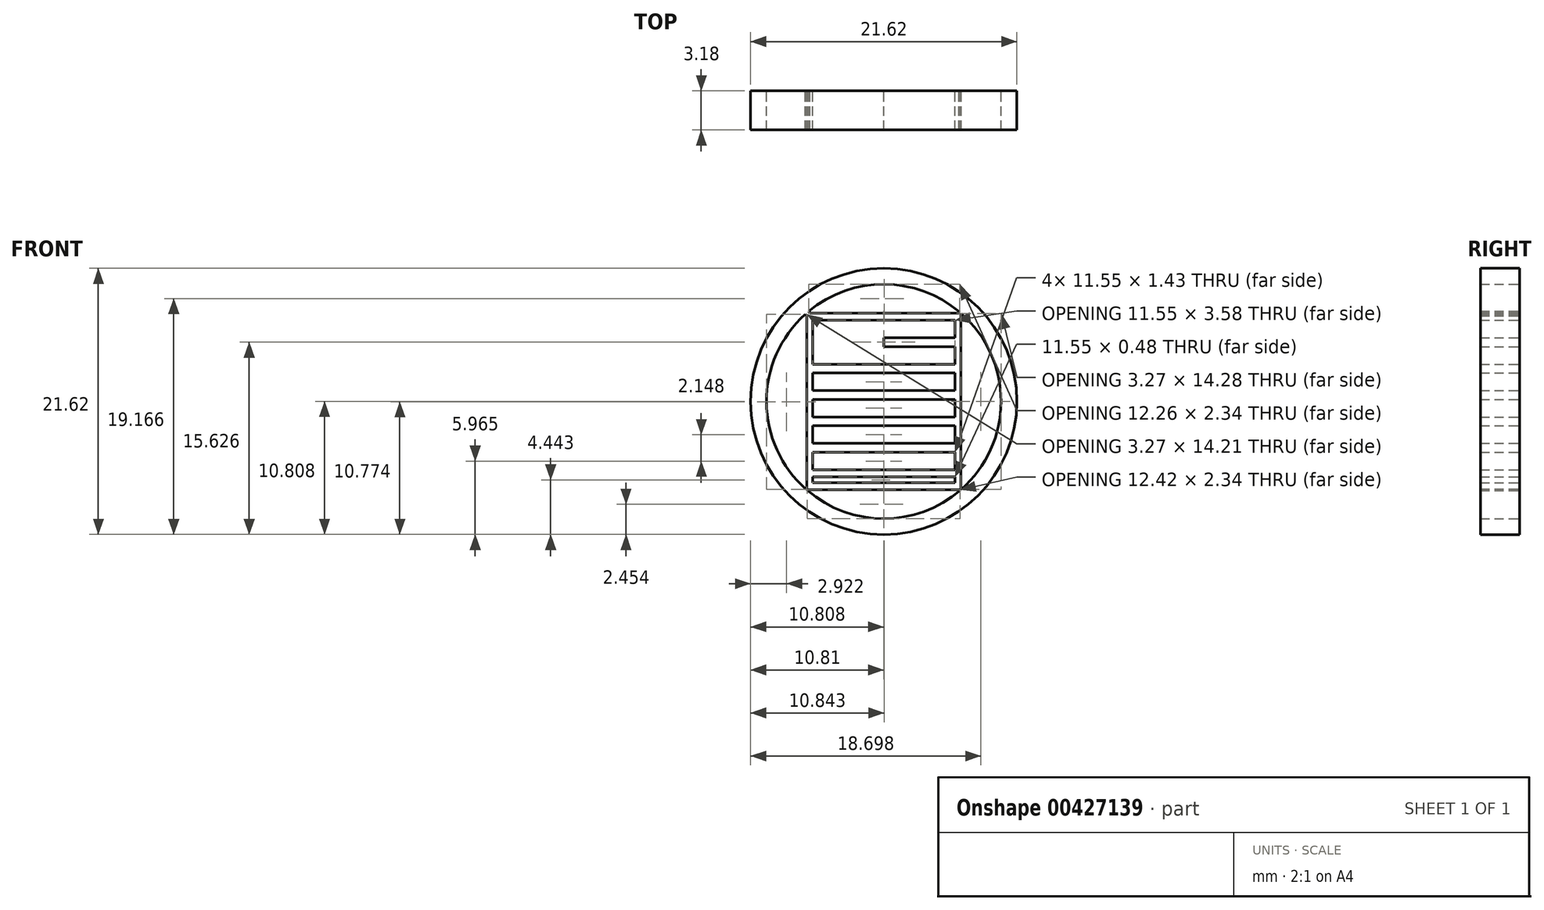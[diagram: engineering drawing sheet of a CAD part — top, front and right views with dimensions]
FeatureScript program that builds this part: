
annotation { "Feature Type Name" : "Feature", "Feature Type Description" : "" }
export const myFeature = defineFeature(function(context is Context, id is Id, definition is map)
    precondition{}
    {
        {
            var Q0;
            Q0=qCreatedBy(makeId("Front.planeOp"),FACE);
            var sketch = newSketch(context, id + "F0", { "sketchPlane" : qUnion([Q0])});
            skCircle(sketch, "E0", {"center": v(0, 0) * mm, "radius": 9.53 * mm});
            skCircle(sketch, "E1", {"center": v(0, 0) * mm, "radius": 10.81 * mm});
            skLineSegment(sketch, "E2", {"start": v(0, 9.53) * mm, "end": v(0, -9.53) * mm});
            skLineSegment(sketch, "E3", {"start": v(-9.53, 0) * mm, "end": v(9.53, 0) * mm});
            skLineSegment(sketch, "E4", {"start": v(-6.25, 7.19) * mm, "end": v(-6.25, -7.19) * mm});
            skLineSegment(sketch, "E5", {"start": v(-6.25, -7.19) * mm, "end": v(6.25, -7.19) * mm});
            skLineSegment(sketch, "E6", {"start": v(6.25, -7.19) * mm, "end": v(6.25, 7.19) * mm});
            skLineSegment(sketch, "E7", {"start": v(6.25, 7.19) * mm, "end": v(-6.25, 7.19) * mm});
            skLineSegment(sketch, "E8", {"start": v(-6.25, 7.19) * mm, "end": v(-5.78, 6.6) * mm});
            skLineSegment(sketch, "E9", {"start": v(-5.78, 6.6) * mm, "end": v(-5.78, -6.6) * mm});
            skLineSegment(sketch, "E10", {"start": v(-5.78, -6.6) * mm, "end": v(-6.25, -7.19) * mm});
            skLineSegment(sketch, "E11", {"start": v(-5.78, -6.6) * mm, "end": v(5.78, -6.6) * mm});
            skLineSegment(sketch, "E12", {"start": v(5.78, -6.6) * mm, "end": v(6.25, -7.19) * mm});
            skLineSegment(sketch, "E13", {"start": v(5.78, -6.6) * mm, "end": v(5.78, 6.6) * mm});
            skLineSegment(sketch, "E14", {"start": v(5.78, 6.6) * mm, "end": v(6.25, 7.19) * mm});
            skLineSegment(sketch, "E15", {"start": v(5.78, 6.6) * mm, "end": v(-5.78, 6.6) * mm});
            skLineSegment(sketch, "E16", {"start": v(-5.78, 5.89) * mm, "end": v(5.78, 5.89) * mm});
            skLineSegment(sketch, "E17", {"start": v(-5.78, 5.17) * mm, "end": v(5.78, 5.17) * mm});
            skLineSegment(sketch, "E18", {"start": v(-5.78, 5.89) * mm, "end": v(-5.78, 5.17) * mm});
            skLineSegment(sketch, "E19", {"start": v(-5.78, 5.89) * mm, "end": v(-5.78, 6.6) * mm});
            skLineSegment(sketch, "E20", {"start": v(-5.78, 4.46) * mm, "end": v(5.78, 4.46) * mm});
            skLineSegment(sketch, "E21", {"start": v(-5.78, 5.17) * mm, "end": v(-5.78, 4.46) * mm});
            skLineSegment(sketch, "E22", {"start": v(-5.78, 3.74) * mm, "end": v(5.78, 3.74) * mm});
            skLineSegment(sketch, "E23", {"start": v(-5.78, 4.46) * mm, "end": v(-5.78, 3.74) * mm});
            skLineSegment(sketch, "E24", {"start": v(-5.78, 3.03) * mm, "end": v(5.78, 3.03) * mm});
            skLineSegment(sketch, "E25", {"start": v(-5.78, 2.31) * mm, "end": v(5.78, 2.31) * mm});
            skLineSegment(sketch, "E26", {"start": v(-5.78, 1.6) * mm, "end": v(5.78, 1.6) * mm});
            skLineSegment(sketch, "E27", {"start": v(-5.78, 0.88) * mm, "end": v(5.78, 0.88) * mm});
            skLineSegment(sketch, "E28", {"start": v(-5.78, 0.16) * mm, "end": v(5.78, 0.16) * mm});
            skLineSegment(sketch, "E29", {"start": v(-5.78, -0.55) * mm, "end": v(5.78, -0.55) * mm});
            skLineSegment(sketch, "E30", {"start": v(-5.78, -1.27) * mm, "end": v(5.78, -1.27) * mm});
            skLineSegment(sketch, "E31", {"start": v(-5.78, -1.98) * mm, "end": v(5.78, -1.98) * mm});
            skLineSegment(sketch, "E32", {"start": v(-5.78, -2.7) * mm, "end": v(5.78, -2.7) * mm});
            skLineSegment(sketch, "E33", {"start": v(-5.78, -3.41) * mm, "end": v(5.78, -3.41) * mm});
            skLineSegment(sketch, "E34", {"start": v(-5.78, -4.13) * mm, "end": v(5.78, -4.13) * mm});
            skLineSegment(sketch, "E35", {"start": v(-5.78, -4.84) * mm, "end": v(5.78, -4.84) * mm});
            skLineSegment(sketch, "E36", {"start": v(-5.78, -5.56) * mm, "end": v(5.78, -5.56) * mm});
            skLineSegment(sketch, "E37", {"start": v(-6.25, 6.94) * mm, "end": v(-6.39, 7.07) * mm});
            skLineSegment(sketch, "E38", {"start": v(-6.1, 7.32) * mm, "end": v(-5.99, 7.19) * mm});
            skLineSegment(sketch, "E39", {"start": v(6.09, 7.19) * mm, "end": v(6.16, 7.26) * mm});
            skLineSegment(sketch, "E40", {"start": v(6.25, 7.07) * mm, "end": v(6.3, 7.14) * mm});
            skLineSegment(sketch, "E41", {"start": v(6.16, -7.19) * mm, "end": v(6.2, -7.22) * mm});
            skLineSegment(sketch, "E42", {"start": v(6.25, -7.1) * mm, "end": v(6.3, -7.14) * mm});
            skLineSegment(sketch, "E43", {"start": v(-6.25, -7.1) * mm, "end": v(-6.3, -7.14) * mm});
            skLineSegment(sketch, "E44", {"start": v(-6.18, -7.19) * mm, "end": v(-6.21, -7.22) * mm});
            skLineSegment(sketch, "E45", {"start": v(5.78, -6.13) * mm, "end": v(-5.78, -6.13) * mm});
            skSolve(sketch);
        }
        {
            var Q0;
            {var subQ5=sQuery(id+"F0.wireOp",EDGE,"E21");Q0=makeQuery(id+"F0.imprint","IMPRINT",FACE,{"disambiguationData":[TD([[makeQuery(id+"F0.imprint","IMPRINT",EDGE,{"derivedFrom":subQ5}),1.0]])]});}
            var Q1;
            {var subQ0=sQuery(id+"F0.wireOp",EDGE,"E17");var subQ1=sQuery(id+"F0.wireOp",EDGE,"E2");var subQ2=makeQuery(id+"F0.imprint","INTERSECT",VERTEX,{"derivedFrom":[subQ1,subQ0]});Q1=makeQuery(id+"F0.imprint","IMPRINT",FACE,{"disambiguationData":[TD([[makeQuery(id+"F0.imprint","IMPRINT",EDGE,{"disambiguationData":[TD([[subQ2,-1.0]])],"derivedFrom":subQ1}),1.0]])]});}
            var Q2;
            {var subQ0=sQuery(id+"F0.wireOp",EDGE,"E24");var subQ1=sQuery(id+"F0.wireOp",EDGE,"E2");var subQ2=makeQuery(id+"F0.imprint","INTERSECT",VERTEX,{"derivedFrom":[subQ1,subQ0]});Q2=makeQuery(id+"F0.imprint","IMPRINT",FACE,{"disambiguationData":[TD([[makeQuery(id+"F0.imprint","IMPRINT",EDGE,{"disambiguationData":[TD([[subQ2,-1.0]])],"derivedFrom":subQ1}),-1.0]])]});}
            var Q3;
            {var subQ0=sQuery(id+"F0.wireOp",EDGE,"E24");var subQ1=sQuery(id+"F0.wireOp",EDGE,"E2");var subQ2=makeQuery(id+"F0.imprint","INTERSECT",VERTEX,{"derivedFrom":[subQ1,subQ0]});Q3=makeQuery(id+"F0.imprint","IMPRINT",FACE,{"disambiguationData":[TD([[makeQuery(id+"F0.imprint","IMPRINT",EDGE,{"disambiguationData":[TD([[subQ2,-1.0]])],"derivedFrom":subQ1}),1.0]])]});}
            var Q4;
            {var subQ0=sQuery(id+"F0.wireOp",EDGE,"E27");var subQ1=sQuery(id+"F0.wireOp",EDGE,"E2");var subQ2=makeQuery(id+"F0.imprint","INTERSECT",VERTEX,{"derivedFrom":[subQ1,subQ0]});Q4=makeQuery(id+"F0.imprint","IMPRINT",FACE,{"disambiguationData":[TD([[makeQuery(id+"F0.imprint","IMPRINT",EDGE,{"disambiguationData":[TD([[subQ2,-1.0]])],"derivedFrom":subQ1}),-1.0]])]});}
            var Q5;
            {var subQ0=sQuery(id+"F0.wireOp",EDGE,"E27");var subQ1=sQuery(id+"F0.wireOp",EDGE,"E2");var subQ2=makeQuery(id+"F0.imprint","INTERSECT",VERTEX,{"derivedFrom":[subQ1,subQ0]});Q5=makeQuery(id+"F0.imprint","IMPRINT",FACE,{"disambiguationData":[TD([[makeQuery(id+"F0.imprint","IMPRINT",EDGE,{"disambiguationData":[TD([[subQ2,-1.0]])],"derivedFrom":subQ1}),1.0]])]});}
            var Q6;
            {var subQ0=sQuery(id+"F0.wireOp",EDGE,"E30");var subQ1=sQuery(id+"F0.wireOp",EDGE,"E2");var subQ2=makeQuery(id+"F0.imprint","INTERSECT",VERTEX,{"derivedFrom":[subQ1,subQ0]});Q6=makeQuery(id+"F0.imprint","IMPRINT",FACE,{"disambiguationData":[TD([[makeQuery(id+"F0.imprint","IMPRINT",EDGE,{"disambiguationData":[TD([[subQ2,-1.0]])],"derivedFrom":subQ1}),-1.0]])]});}
            var Q7;
            {var subQ0=sQuery(id+"F0.wireOp",EDGE,"E30");var subQ1=sQuery(id+"F0.wireOp",EDGE,"E2");var subQ2=makeQuery(id+"F0.imprint","INTERSECT",VERTEX,{"derivedFrom":[subQ1,subQ0]});Q7=makeQuery(id+"F0.imprint","IMPRINT",FACE,{"disambiguationData":[TD([[makeQuery(id+"F0.imprint","IMPRINT",EDGE,{"disambiguationData":[TD([[subQ2,-1.0]])],"derivedFrom":subQ1}),1.0]])]});}
            var Q8;
            {var subQ0=sQuery(id+"F0.wireOp",EDGE,"E33");var subQ1=sQuery(id+"F0.wireOp",EDGE,"E2");var subQ2=makeQuery(id+"F0.imprint","INTERSECT",VERTEX,{"derivedFrom":[subQ1,subQ0]});Q8=makeQuery(id+"F0.imprint","IMPRINT",FACE,{"disambiguationData":[TD([[makeQuery(id+"F0.imprint","IMPRINT",EDGE,{"disambiguationData":[TD([[subQ2,-1.0]])],"derivedFrom":subQ1}),1.0]])]});}
            var Q9;
            {var subQ0=sQuery(id+"F0.wireOp",EDGE,"E33");var subQ1=sQuery(id+"F0.wireOp",EDGE,"E2");var subQ2=makeQuery(id+"F0.imprint","INTERSECT",VERTEX,{"derivedFrom":[subQ1,subQ0]});Q9=makeQuery(id+"F0.imprint","IMPRINT",FACE,{"disambiguationData":[TD([[makeQuery(id+"F0.imprint","IMPRINT",EDGE,{"disambiguationData":[TD([[subQ2,-1.0]])],"derivedFrom":subQ1}),-1.0]])]});}
            var Q10;
            {var subQ0=sQuery(id+"F0.wireOp",EDGE,"E36");var subQ1=sQuery(id+"F0.wireOp",EDGE,"E2");var subQ2=makeQuery(id+"F0.imprint","INTERSECT",VERTEX,{"derivedFrom":[subQ1,subQ0]});Q10=makeQuery(id+"F0.imprint","IMPRINT",FACE,{"disambiguationData":[TD([[makeQuery(id+"F0.imprint","IMPRINT",EDGE,{"disambiguationData":[TD([[subQ2,-1.0]])],"derivedFrom":subQ1}),-1.0]])]});}
            var Q11;
            {var subQ0=sQuery(id+"F0.wireOp",EDGE,"E36");var subQ1=sQuery(id+"F0.wireOp",EDGE,"E2");var subQ2=makeQuery(id+"F0.imprint","INTERSECT",VERTEX,{"derivedFrom":[subQ1,subQ0]});Q11=makeQuery(id+"F0.imprint","IMPRINT",FACE,{"disambiguationData":[TD([[makeQuery(id+"F0.imprint","IMPRINT",EDGE,{"disambiguationData":[TD([[subQ2,-1.0]])],"derivedFrom":subQ1}),1.0]])]});}
            var Q12;
            {var subQ5=sQuery(id+"F0.wireOp",EDGE,"E12");Q12=makeQuery(id+"F0.imprint","IMPRINT",FACE,{"disambiguationData":[TD([[makeQuery(id+"F0.imprint","IMPRINT",EDGE,{"derivedFrom":subQ5}),1.0]])]});}
            var Q13;
            {var subQ13=sQuery(id+"F0.wireOp",EDGE,"E14");Q13=makeQuery(id+"F0.imprint","IMPRINT",FACE,{"disambiguationData":[TD([[makeQuery(id+"F0.imprint","IMPRINT",EDGE,{"derivedFrom":subQ13}),-1.0]])]});}
            var Q14;
            {var subQ4=sQuery(id+"F0.wireOp",EDGE,"E14");Q14=makeQuery(id+"F0.imprint","IMPRINT",FACE,{"disambiguationData":[TD([[makeQuery(id+"F0.imprint","IMPRINT",EDGE,{"derivedFrom":subQ4}),1.0]])]});}
            var Q15;
            {var subQ0=sQuery(id+"F0.wireOp",EDGE,"E8");Q15=makeQuery(id+"F0.imprint","IMPRINT",FACE,{"disambiguationData":[TD([[makeQuery(id+"F0.imprint","IMPRINT",EDGE,{"derivedFrom":subQ0}),1.0]])]});}
            var Q16;
            {var subQ11=sQuery(id+"F0.wireOp",EDGE,"E8");Q16=makeQuery(id+"F0.imprint","IMPRINT",FACE,{"disambiguationData":[TD([[makeQuery(id+"F0.imprint","IMPRINT",EDGE,{"derivedFrom":subQ11}),-1.0]])]});}
            var Q17;
            {var subQ6=sQuery(id+"F0.wireOp",EDGE,"E10");Q17=makeQuery(id+"F0.imprint","IMPRINT",FACE,{"disambiguationData":[TD([[makeQuery(id+"F0.imprint","IMPRINT",EDGE,{"derivedFrom":subQ6}),-1.0]])]});}
            var Q18;
            {var subQ0=sQuery(id+"F0.wireOp",EDGE,"E10");Q18=makeQuery(id+"F0.imprint","IMPRINT",FACE,{"disambiguationData":[TD([[makeQuery(id+"F0.imprint","IMPRINT",EDGE,{"derivedFrom":subQ0}),1.0]])]});}
            var Q19;
            {var subQ0=sQuery(id+"F0.wireOp",EDGE,"E12");Q19=makeQuery(id+"F0.imprint","IMPRINT",FACE,{"disambiguationData":[TD([[makeQuery(id+"F0.imprint","IMPRINT",EDGE,{"derivedFrom":subQ0}),-1.0]])]});}
            var Q20;
            {var subQ3=sQuery(id+"F0.wireOp",EDGE,"E38");Q20=makeQuery(id+"F0.imprint","IMPRINT",FACE,{"disambiguationData":[TD([[makeQuery(id+"F0.imprint","IMPRINT",EDGE,{"derivedFrom":subQ3}),-1.0]])]});}
            var Q21;
            {var subQ3=sQuery(id+"F0.wireOp",EDGE,"E37");Q21=makeQuery(id+"F0.imprint","IMPRINT",FACE,{"disambiguationData":[TD([[makeQuery(id+"F0.imprint","IMPRINT",EDGE,{"derivedFrom":subQ3}),-1.0]])]});}
            var Q22;
            Q22=makeQuery(id+"F0.imprint","IMPRINT",FACE,{"disambiguationData":[TD([[makeQuery(id+"F0.imprint","IMPRINT",EDGE,{"derivedFrom":sQuery(id+"F0.wireOp",EDGE,"E1")}),1.0]])]});
            var Q23;
            {var subQ3=sQuery(id+"F0.wireOp",EDGE,"E39");Q23=makeQuery(id+"F0.imprint","IMPRINT",FACE,{"disambiguationData":[TD([[makeQuery(id+"F0.imprint","IMPRINT",EDGE,{"derivedFrom":subQ3}),-1.0]])]});}
            var Q24;
            {var subQ3=sQuery(id+"F0.wireOp",EDGE,"E40");Q24=makeQuery(id+"F0.imprint","IMPRINT",FACE,{"disambiguationData":[TD([[makeQuery(id+"F0.imprint","IMPRINT",EDGE,{"derivedFrom":subQ3}),1.0]])]});}
            var Q25;
            {var subQ3=sQuery(id+"F0.wireOp",EDGE,"E42");Q25=makeQuery(id+"F0.imprint","IMPRINT",FACE,{"disambiguationData":[TD([[makeQuery(id+"F0.imprint","IMPRINT",EDGE,{"derivedFrom":subQ3}),-1.0]])]});}
            var Q26;
            {var subQ3=sQuery(id+"F0.wireOp",EDGE,"E41");Q26=makeQuery(id+"F0.imprint","IMPRINT",FACE,{"disambiguationData":[TD([[makeQuery(id+"F0.imprint","IMPRINT",EDGE,{"derivedFrom":subQ3}),1.0]])]});}
            var Q27;
            {var subQ3=sQuery(id+"F0.wireOp",EDGE,"E43");Q27=makeQuery(id+"F0.imprint","IMPRINT",FACE,{"disambiguationData":[TD([[makeQuery(id+"F0.imprint","IMPRINT",EDGE,{"derivedFrom":subQ3}),1.0]])]});}
            var Q28;
            {var subQ3=sQuery(id+"F0.wireOp",EDGE,"E44");Q28=makeQuery(id+"F0.imprint","IMPRINT",FACE,{"disambiguationData":[TD([[makeQuery(id+"F0.imprint","IMPRINT",EDGE,{"derivedFrom":subQ3}),-1.0]])]});}
            extrude(context, id + "F1", {"entities" : qUnion([Q0, Q1, Q2, Q3, Q4, Q5, Q6, Q7, Q8, Q9, Q10, Q11, Q12, Q13, Q14, Q15, Q16, Q17, Q18, Q19, Q20, Q21, Q22, Q23, Q24, Q25, Q26, Q27, Q28]), "depth" : 3.17 * mm});
        }
    });
